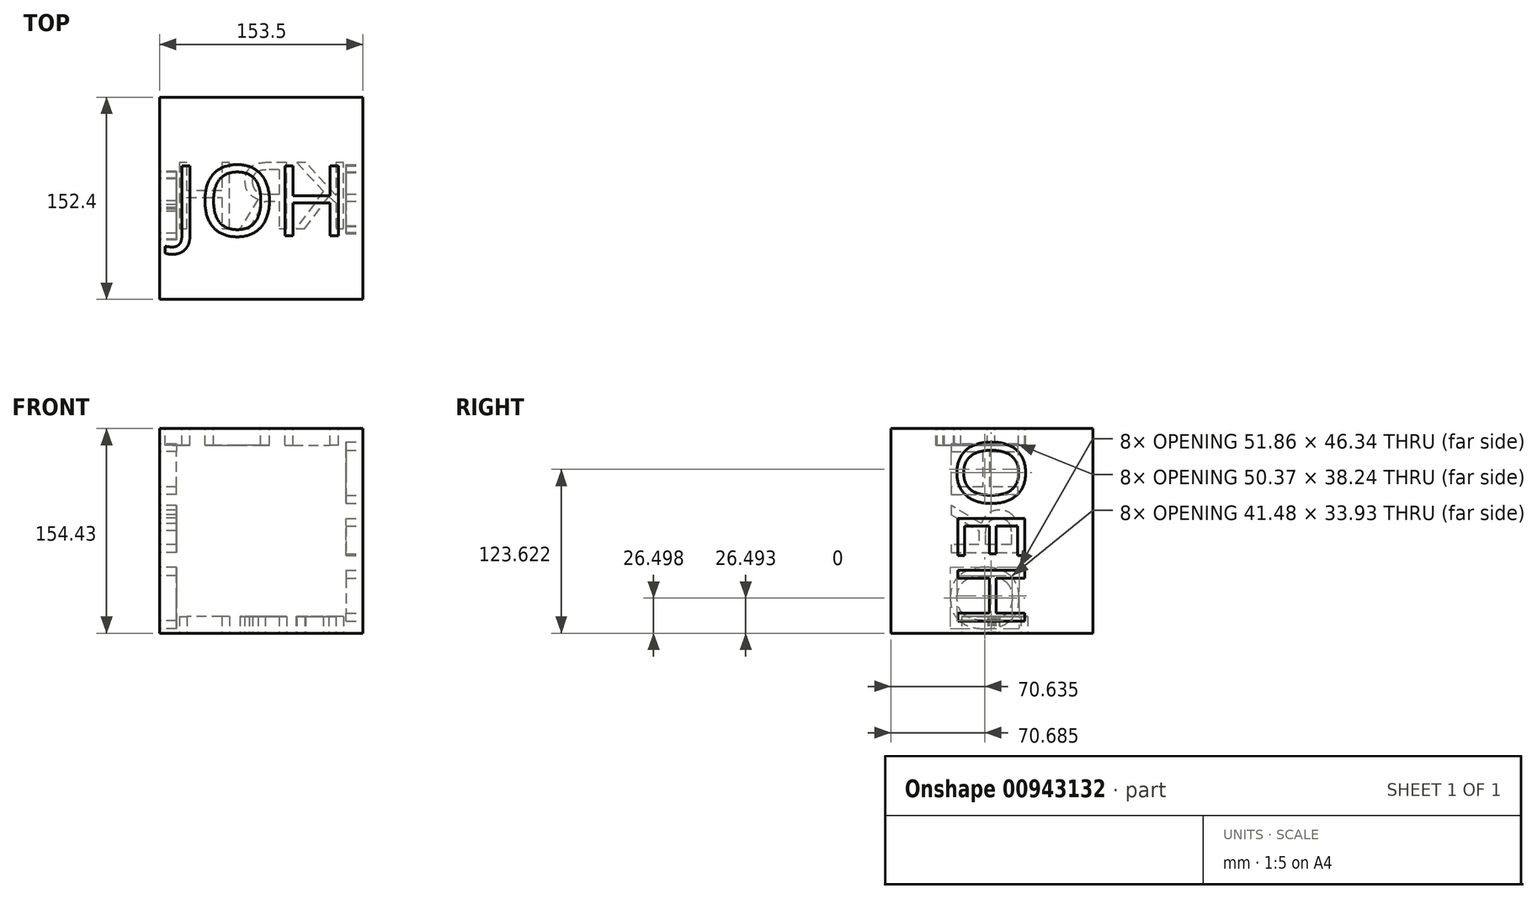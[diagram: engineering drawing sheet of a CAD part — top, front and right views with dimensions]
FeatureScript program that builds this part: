
annotation { "Feature Type Name" : "Feature", "Feature Type Description" : "" }
export const myFeature = defineFeature(function(context is Context, id is Id, definition is map)
    precondition{}
    {
        {
            var Q0;
            Q0=qCreatedBy(makeId("Top.planeOp"),FACE);
            var sketch = newSketch(context, id + "F0", { "sketchPlane" : qUnion([Q0])});
            skLineSegment(sketch, "E0.bottom", {"start": v(0, 0) * mm, "end": v(-153.5, 0) * mm});
            skLineSegment(sketch, "E0.top", {"start": v(0, 152.4) * mm, "end": v(-153.5, 152.4) * mm});
            skLineSegment(sketch, "E0.left", {"start": v(0, 0) * mm, "end": v(0, 152.4) * mm});
            skLineSegment(sketch, "E0.right", {"start": v(-153.5, 0) * mm, "end": v(-153.5, 152.4) * mm});
            skSolve(sketch);
        }
        {
            var Q0;
            Q0=makeQuery(id+"F0.imprint","IMPRINT",FACE,{"disambiguationData":[TD([[makeQuery(id+"F0.imprint","IMPRINT",EDGE,{"derivedFrom":sQuery(id+"F0.wireOp",EDGE,"E0.bottom")}),-1.0]])]});
            extrude(context, id + "F1", {"entities" : qUnion([Q0]), "depth" : 154.43 * mm, "offsetDistance" : 25.4 * mm});
        }
        {
            var Q0;
            Q0=makeQuery(id+"F1.opExtrude","CAP_FACE",FACE,{"disambiguationData":[OSD([sQuery(id+"F0.wireOp",EDGE,"E0.bottom"),sQuery(id+"F0.wireOp",EDGE,"E0.top"),sQuery(id+"F0.wireOp",EDGE,"E0.left"),sQuery(id+"F0.wireOp",EDGE,"E0.right")])],"isStart":false});
            var sketch = newSketch(context, id + "F2", { "sketchPlane" : qUnion([Q0])});
            skText(sketch, "E1", { "text": "JOH\n", "fontName": "OpenSans-Regular.ttf"});
            const initialGuessF2  = {"E1": [-0.1436, 0.04787, 1, 0, 0.05334]};
            skSetInitialGuess(sketch, initialGuessF2);
            skSolve(sketch);
        }
        {
            var Q0;
            Q0=makeQuery(id+"F2.imprint","IMPRINT",FACE,{"disambiguationData":[TD([[makeQuery(id+"F2.imprint","IMPRINT",EDGE,{"derivedFrom":sQuery(id+"F2.wireOp",EDGE,"E1.sketch_text.stroke-0")}),-1.0]])]});
            var Q1;
            Q1=makeQuery(id+"F2.imprint","IMPRINT",FACE,{"disambiguationData":[TD([[makeQuery(id+"F2.imprint","IMPRINT",EDGE,{"derivedFrom":sQuery(id+"F2.wireOp",EDGE,"E1.sketch_text.stroke-10")}),-1.0]])]});
            var Q2;
            Q2=makeQuery(id+"F2.imprint","IMPRINT",FACE,{"disambiguationData":[TD([[makeQuery(id+"F2.imprint","IMPRINT",EDGE,{"derivedFrom":sQuery(id+"F2.wireOp",EDGE,"E1.sketch_text.stroke-26")}),-1.0]])]});
            extrude(context, id + "F3", {"entities" : qUnion([Q0, Q1, Q2]), "operationType" : NewBodyOperationType.REMOVE, "oppositeDirection" : true, "depth" : 12.7 * mm, "offsetDistance" : 25.4 * mm});
        }
        {
            var Q0;
            Q0=makeQuery(id+"F1.opExtrude","SWEPT_FACE",FACE,{"disambiguationData":[OSD([sQuery(id+"F0.wireOp",EDGE,"E0.left")])]});
            var sketch = newSketch(context, id + "F4", { "sketchPlane" : qUnion([Q0])});
            skText(sketch, "E2", { "text": "OEH", "fontName": "OpenSans-Regular.ttf"});
            const initialGuessF4  = {"E2": [0.05037, 0.14848, 0, -1, 0.0508]};
            skSetInitialGuess(sketch, initialGuessF4);
            skSolve(sketch);
        }
        {
            var Q0;
            Q0 = qSketchRegion(id + "F4", true);
            extrude(context, id + "F5", {"entities" : qUnion([Q0]), "operationType" : NewBodyOperationType.REMOVE, "oppositeDirection" : true, "depth" : 12.7 * mm, "offsetDistance" : 25.4 * mm});
        }
        {
            var Q0;
            Q0=makeQuery(id+"F1.opExtrude","CAP_FACE",FACE,{"disambiguationData":[OSD([sQuery(id+"F0.wireOp",EDGE,"E0.bottom"),sQuery(id+"F0.wireOp",EDGE,"E0.top"),sQuery(id+"F0.wireOp",EDGE,"E0.left"),sQuery(id+"F0.wireOp",EDGE,"E0.right")])],"isStart":true});
            var sketch = newSketch(context, id + "F6", { "sketchPlane" : qUnion([Q0])});
            skText(sketch, "E3", { "text": "KRH\n", "fontName": "OpenSans-Regular.ttf"});
            const initialGuessF6  = {"E3": [-0.00788, -0.05326, -1, 0, 0.05032]};
            skSetInitialGuess(sketch, initialGuessF6);
            skSolve(sketch);
        }
        {
            var Q0;
            Q0 = qSketchRegion(id + "F6", true);
            extrude(context, id + "F7", {"entities" : qUnion([Q0]), "operationType" : NewBodyOperationType.REMOVE, "oppositeDirection" : true, "depth" : 12.7 * mm, "offsetDistance" : 25.4 * mm});
        }
        {
            var Q0;
            Q0=makeQuery(id+"F1.opExtrude","SWEPT_FACE",FACE,{"disambiguationData":[OSD([sQuery(id+"F0.wireOp",EDGE,"E0.right")])]});
            var sketch = newSketch(context, id + "F8", { "sketchPlane" : qUnion([Q0])});
            skText(sketch, "E4", { "text": "ORH", "fontName": "OpenSans-Regular.ttf"});
            const initialGuessF8  = {"E4": [-0.04545, -0.00098, 0, 1, 0.0508]};
            skSetInitialGuess(sketch, initialGuessF8);
            skSolve(sketch);
        }
        {
            var Q0;
            Q0=makeQuery(id+"F8.imprint","IMPRINT",FACE,{"disambiguationData":[TD([[makeQuery(id+"F8.imprint","IMPRINT",EDGE,{"derivedFrom":sQuery(id+"F8.wireOp",EDGE,"E4.sketch_text.stroke-34")}),-1.0]])]});
            var Q1;
            Q1=makeQuery(id+"F8.imprint","IMPRINT",FACE,{"disambiguationData":[TD([[makeQuery(id+"F8.imprint","IMPRINT",EDGE,{"derivedFrom":sQuery(id+"F8.wireOp",EDGE,"E4.sketch_text.stroke-16")}),-1.0]])]});
            var Q2;
            Q2=makeQuery(id+"F8.imprint","IMPRINT",FACE,{"disambiguationData":[TD([[makeQuery(id+"F8.imprint","IMPRINT",EDGE,{"derivedFrom":sQuery(id+"F8.wireOp",EDGE,"E4.sketch_text.stroke-0")}),-1.0]])]});
            extrude(context, id + "F9", {"entities" : qUnion([Q0, Q1, Q2]), "operationType" : NewBodyOperationType.REMOVE, "oppositeDirection" : true, "depth" : 12.7 * mm, "offsetDistance" : 25.4 * mm});
        }
    });
